# Revit family: КРД_Eng
name_source: partatom
category: Duct Accessories
units: mm (PartAtom-declared; Revit-internal decimal feet)

## family parameters
Always vertical = Yes
Cut with Voids When Loaded = No
Part Type = Attaches To
Round Connector Dimension = Use Diameter
Shared = No
Work Plane-Based = No

## types (25) — shared parameters
00_20_Manufacturer = Vents
00_20_Name = Pressure control valve
Casing Material = Steel, galvanized
L = 100 mm  [stored 0.328084 ft]
Length = 100 mm  [stored 0.328084 ft]
Load Classification = HVAC
Maintenance zone material = <By Category>
Manufacturer = Vents
Maximum Air Flow = 0.0 L/s
URL = https://ventilation-system.com
zero-valued in all types: Default Elevation

## per-type parameters (varying)
| type | B | H | Height | Hole | Width | With right flange | a | a1 | p1 |
| KRD-1-1000х1000 | 1000 mm  [stored 3.28084 ft] | 1000 mm  [stored 3.28084 ft] | 1000 mm  [stored 3.28084 ft] | Yes | 1000 mm  [stored 3.28084 ft] | No | 15 mm  [stored 0.0492126 ft] | 30 mm  [stored 0.0984252 ft] | 400 mm  [stored 1.31234 ft] |
| KRD-1-425х425 | 425 mm  [stored 1.39436 ft] | 425 mm  [stored 1.39436 ft] | 425 mm  [stored 1.39436 ft] | Yes | 425 mm  [stored 1.39436 ft] | No | 10 mm  [stored 0.0328084 ft] | 20 mm  [stored 0.0656168 ft] | 170 mm  [stored 0.557743 ft] |
| KRD-1-300х300 | 300 mm | 300 mm | 300 mm | No | 300 mm | No | 10 mm  [stored 0.0328084 ft] | 20 mm  [stored 0.0656168 ft] | 120 mm |
| KRD-1-550х550 | 550 mm | 550 mm | 550 mm | Yes | 550 mm | No | 15 mm  [stored 0.0492126 ft] | 30 mm  [stored 0.0984252 ft] | 220 mm  [stored 0.721785 ft] |
| KRD-1-600х175 | 600 mm | 175 mm  [stored 0.574147 ft] | 175 mm  [stored 0.574147 ft] | Yes | 600 mm | No | 10 mm  [stored 0.0328084 ft] | 20 mm  [stored 0.0656168 ft] | 70 mm  [stored 0.229659 ft] |
| KRD-1-700х300 | 700 mm  [stored 2.29659 ft] | 300 mm | 300 mm | Yes | 700 mm  [stored 2.29659 ft] | No | 10 mm  [stored 0.0328084 ft] | 20 mm  [stored 0.0656168 ft] | 120 mm |
| KRD-1-800х800 | 800 mm  [stored 2.62467 ft] | 800 mm  [stored 2.62467 ft] | 800 mm  [stored 2.62467 ft] | Yes | 800 mm  [stored 2.62467 ft] | No | 15 mm  [stored 0.0492126 ft] | 30 mm  [stored 0.0984252 ft] | 320 mm  [stored 1.04987 ft] |
| KRD-1-900х900 | 900 mm  [stored 2.95276 ft] | 900 mm  [stored 2.95276 ft] | 900 mm  [stored 2.95276 ft] | Yes | 900 mm  [stored 2.95276 ft] | No | 15 mm  [stored 0.0492126 ft] | 30 mm  [stored 0.0984252 ft] | 360 mm  [stored 1.1811 ft] |
| KRD-1-200х300 | 200 mm  [stored 0.656168 ft] | 300 mm | 300 mm | No | 200 mm  [stored 0.656168 ft] | No | 10 mm  [stored 0.0328084 ft] | 20 mm  [stored 0.0656168 ft] | 120 mm |
| KRD-1-300х175 | 300 mm | 175 mm  [stored 0.574147 ft] | 175 mm  [stored 0.574147 ft] | No | 300 mm | No | 10 mm  [stored 0.0328084 ft] | 20 mm  [stored 0.0656168 ft] | 70 mm  [stored 0.229659 ft] |
| KRD-1-675х675 | 675 mm  [stored 2.21457 ft] | 675 mm  [stored 2.21457 ft] | 675 mm  [stored 2.21457 ft] | Yes | 675 mm  [stored 2.21457 ft] | No | 15 mm  [stored 0.0492126 ft] | 30 mm  [stored 0.0984252 ft] | 270 mm  [stored 0.885827 ft] |
| KRD-1-800х650 | 800 mm  [stored 2.62467 ft] | 650 mm  [stored 2.13255 ft] | 650 mm  [stored 2.13255 ft] | Yes | 800 mm  [stored 2.62467 ft] | No | 15 mm  [stored 0.0492126 ft] | 30 mm  [stored 0.0984252 ft] | 260 mm  [stored 0.853018 ft] |
| KRD-1-200х200 | 200 mm  [stored 0.656168 ft] | 200 mm  [stored 0.656168 ft] | 200 mm  [stored 0.656168 ft] | No | 200 mm  [stored 0.656168 ft] | No | 10 mm  [stored 0.0328084 ft] | 20 mm  [stored 0.0656168 ft] | 80 mm  [stored 0.262467 ft] |
| KRD-2-200х200 | 200 mm  [stored 0.656168 ft] | 200 mm  [stored 0.656168 ft] | 200 mm  [stored 0.656168 ft] | No | 200 mm  [stored 0.656168 ft] | Yes | 10 mm  [stored 0.0328084 ft] | 20 mm  [stored 0.0656168 ft] | 80 mm  [stored 0.262467 ft] |
| KRD-2-300х300 | 300 mm | 300 mm | 300 mm | No | 300 mm | Yes | 10 mm  [stored 0.0328084 ft] | 20 mm  [stored 0.0656168 ft] | 120 mm |
| KRD-2-400х400 | 400 mm  [stored 1.31234 ft] | 400 mm  [stored 1.31234 ft] | 400 mm  [stored 1.31234 ft] | Yes | 400 mm  [stored 1.31234 ft] | Yes | 10 mm  [stored 0.0328084 ft] | 20 mm  [stored 0.0656168 ft] | 160 mm  [stored 0.524934 ft] |
| KRD-1-400х400 | 400 mm  [stored 1.31234 ft] | 400 mm  [stored 1.31234 ft] | 400 mm  [stored 1.31234 ft] | Yes | 400 mm  [stored 1.31234 ft] | No | 10 mm  [stored 0.0328084 ft] | 20 mm  [stored 0.0656168 ft] | 160 mm  [stored 0.524934 ft] |
| KRD-2-500х500 | 500 mm  [stored 1.64042 ft] | 500 mm  [stored 1.64042 ft] | 500 mm  [stored 1.64042 ft] | Yes | 500 mm  [stored 1.64042 ft] | Yes | 10 mm  [stored 0.0328084 ft] | 20 mm  [stored 0.0656168 ft] | 200 mm  [stored 0.656168 ft] |
| KRD-1-500х500 | 500 mm  [stored 1.64042 ft] | 500 mm  [stored 1.64042 ft] | 500 mm  [stored 1.64042 ft] | Yes | 500 mm  [stored 1.64042 ft] | No | 10 mm  [stored 0.0328084 ft] | 20 mm  [stored 0.0656168 ft] | 200 mm  [stored 0.656168 ft] |
| KRD-2-600х600 | 600 mm | 600 mm | 600 mm | Yes | 600 mm | Yes | 15 mm  [stored 0.0492126 ft] | 30 mm  [stored 0.0984252 ft] | 240 mm  [stored 0.787402 ft] |
| KRD-1-600х600 | 600 mm | 600 mm | 600 mm | Yes | 600 mm | No | 15 mm  [stored 0.0492126 ft] | 30 mm  [stored 0.0984252 ft] | 240 mm  [stored 0.787402 ft] |
| KRD-1-700х700 | 700 mm  [stored 2.29659 ft] | 700 mm  [stored 2.29659 ft] | 700 mm  [stored 2.29659 ft] | Yes | 700 mm  [stored 2.29659 ft] | No | 15 mm  [stored 0.0492126 ft] | 30 mm  [stored 0.0984252 ft] | 280 mm  [stored 0.918635 ft] |
| KRD-2-700х700 | 700 mm  [stored 2.29659 ft] | 700 mm  [stored 2.29659 ft] | 700 mm  [stored 2.29659 ft] | Yes | 700 mm  [stored 2.29659 ft] | Yes | 15 mm  [stored 0.0492126 ft] | 30 mm  [stored 0.0984252 ft] | 280 mm  [stored 0.918635 ft] |
| KRD-2-800х800 | 800 mm  [stored 2.62467 ft] | 800 mm  [stored 2.62467 ft] | 800 mm  [stored 2.62467 ft] | Yes | 800 mm  [stored 2.62467 ft] | Yes | 15 mm  [stored 0.0492126 ft] | 30 mm  [stored 0.0984252 ft] | 320 mm  [stored 1.04987 ft] |
| KRD-2-900х900 | 900 mm  [stored 2.95276 ft] | 900 mm  [stored 2.95276 ft] | 900 mm  [stored 2.95276 ft] | Yes | 900 mm  [stored 2.95276 ft] | Yes | 15 mm  [stored 0.0492126 ft] | 30 mm  [stored 0.0984252 ft] | 360 mm  [stored 1.1811 ft] |

note: column(s) folded — value = type name in every type: 00_20_Type

note: [stored X ft] marks values corroborated as IEEE doubles in the binary element streams (Revit-internal decimal feet)
